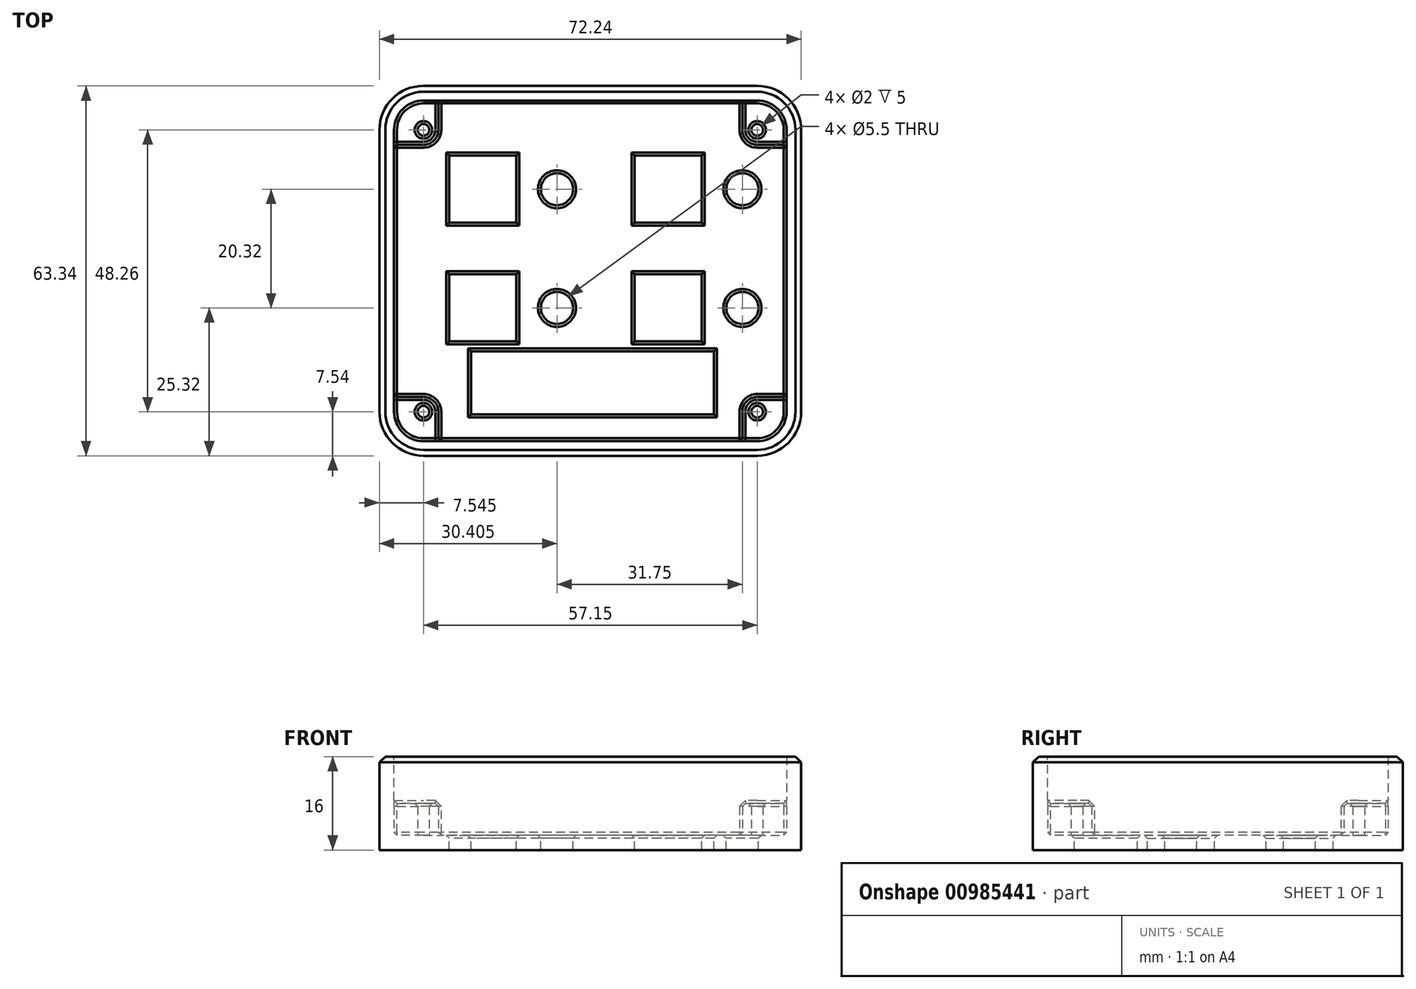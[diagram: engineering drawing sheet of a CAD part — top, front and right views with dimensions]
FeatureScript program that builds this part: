
annotation { "Feature Type Name" : "Feature", "Feature Type Description" : "" }
export const myFeature = defineFeature(function(context is Context, id is Id, definition is map)
    precondition{}
    {
        {
            var Q0;
            Q0=qCreatedBy(makeId("Top.planeOp"),FACE);
            var sketch = newSketch(context, id + "F0", { "sketchPlane" : qUnion([Q0])});
            skLineSegment(sketch, "E0.bottom", {"start": v(-28.57, -31.67) * mm, "end": v(28.58, -31.67) * mm});
            skLineSegment(sketch, "E0.top", {"start": v(-28.57, 31.67) * mm, "end": v(28.58, 31.67) * mm});
            skLineSegment(sketch, "E0.left", {"start": v(-36.11, -24.13) * mm, "end": v(-36.12, 24.13) * mm});
            skLineSegment(sketch, "E0.right", {"start": v(36.12, -24.13) * mm, "end": v(36.11, 24.13) * mm});
            skPoint(sketch, "E0.middle", {"position": v(0, 0) * mm});
            skPoint(sketch, "E1.visualSharp", {"position": v(-36.12, 31.67) * mm});
            skArc(sketch, "E1.filletArc", {"start": v(-28.57, 31.67) * mm, "mid": v(-33.9, 29.46) * mm, "end": v(-36.12, 24.13) * mm});
            skPoint(sketch, "E2.visualSharp", {"position": v(36.11, 31.67) * mm});
            skArc(sketch, "E2.filletArc", {"start": v(36.12, 24.13) * mm, "mid": v(33.9, 29.46) * mm, "end": v(28.58, 31.67) * mm});
            skPoint(sketch, "E3.visualSharp", {"position": v(36.12, -31.67) * mm});
            skArc(sketch, "E3.filletArc", {"start": v(28.58, -31.67) * mm, "mid": v(33.9, -29.46) * mm, "end": v(36.12, -24.13) * mm});
            skPoint(sketch, "E4.visualSharp", {"position": v(-36.11, -31.67) * mm});
            skArc(sketch, "E4.filletArc", {"start": v(-36.11, -24.13) * mm, "mid": v(-33.9, -29.46) * mm, "end": v(-28.57, -31.67) * mm});
            skCircle(sketch, "E5", {"center": v(-28.57, 24.13) * mm, "radius": 1 * mm});
            skCircle(sketch, "E6", {"center": v(28.58, 24.13) * mm, "radius": 1 * mm});
            skCircle(sketch, "E7", {"center": v(28.58, -24.13) * mm, "radius": 1 * mm});
            skCircle(sketch, "E8", {"center": v(-28.57, -24.13) * mm, "radius": 1 * mm});
            skLineSegment(sketch, "E9", {"start": v(-26.04, 31.67) * mm, "end": v(-26.04, 24.13) * mm});
            skLineSegment(sketch, "E10", {"start": v(-28.57, 21.6) * mm, "end": v(-36.11, 21.6) * mm});
            skPoint(sketch, "E11.visualSharp", {"position": v(-26.04, 21.6) * mm});
            skArc(sketch, "E11.filletArc", {"start": v(-28.57, 21.6) * mm, "mid": v(-26.78, 22.33) * mm, "end": v(-26.04, 24.13) * mm});
            skLineSegment(sketch, "E12.MirrorCS", {"start": v(26.04, 31.67) * mm, "end": v(26.04, 24.13) * mm});
            skArc(sketch, "E13.MirrorCS", {"start": v(28.57, 21.6) * mm, "mid": v(26.78, 22.33) * mm, "end": v(26.04, 24.13) * mm});
            skLineSegment(sketch, "E14.MirrorCS", {"start": v(28.57, 21.6) * mm, "end": v(36.11, 21.6) * mm});
            skLineSegment(sketch, "E15.MirrorCS", {"start": v(-28.57, -21.6) * mm, "end": v(-36.11, -21.6) * mm});
            skArc(sketch, "E16.MirrorCS", {"start": v(-28.57, -21.6) * mm, "mid": v(-26.78, -22.33) * mm, "end": v(-26.04, -24.13) * mm});
            skLineSegment(sketch, "E17.MirrorCS", {"start": v(-26.04, -31.67) * mm, "end": v(-26.04, -24.13) * mm});
            skLineSegment(sketch, "E18.MirrorCS", {"start": v(28.57, -21.6) * mm, "end": v(36.11, -21.6) * mm});
            skArc(sketch, "E19.MirrorCS", {"start": v(28.57, -21.6) * mm, "mid": v(26.78, -22.33) * mm, "end": v(26.04, -24.13) * mm});
            skLineSegment(sketch, "E20.MirrorCS", {"start": v(26.04, -31.67) * mm, "end": v(26.04, -24.13) * mm});
            skSolve(sketch);
        }
        {
            var Q0;
            {var subQ0=sQuery(id+"F0.wireOp",EDGE,"E4.filletArc");Q0=makeQuery(id+"F0.imprint","IMPRINT",FACE,{"disambiguationData":[TD([[makeQuery(id+"F0.imprint","IMPRINT",EDGE,{"derivedFrom":subQ0}),1.0]])]});}
            var Q1;
            {var subQ4=sQuery(id+"F0.wireOp",EDGE,"E9");Q1=makeQuery(id+"F0.imprint","IMPRINT",FACE,{"disambiguationData":[TD([[makeQuery(id+"F0.imprint","IMPRINT",EDGE,{"derivedFrom":subQ4}),1.0]])]});}
            var Q2;
            {var subQ0=sQuery(id+"F0.wireOp",EDGE,"E1.filletArc");Q2=makeQuery(id+"F0.imprint","IMPRINT",FACE,{"disambiguationData":[TD([[makeQuery(id+"F0.imprint","IMPRINT",EDGE,{"derivedFrom":subQ0}),1.0]])]});}
            var Q3;
            {var subQ1=sQuery(id+"F0.wireOp",EDGE,"E3.filletArc");Q3=makeQuery(id+"F0.imprint","IMPRINT",FACE,{"disambiguationData":[TD([[makeQuery(id+"F0.imprint","IMPRINT",EDGE,{"derivedFrom":subQ1}),1.0]])]});}
            var Q4;
            {var subQ0=sQuery(id+"F0.wireOp",EDGE,"E2.filletArc");Q4=makeQuery(id+"F0.imprint","IMPRINT",FACE,{"disambiguationData":[TD([[makeQuery(id+"F0.imprint","IMPRINT",EDGE,{"derivedFrom":subQ0}),1.0]])]});}
            var Q5;
            Q5=makeQuery(id+"F0.imprint","IMPRINT",FACE,{"disambiguationData":[TD([[makeQuery(id+"F0.imprint","IMPRINT",EDGE,{"derivedFrom":sQuery(id+"F0.wireOp",EDGE,"E7")}),1.0]])]});
            var Q6;
            Q6=makeQuery(id+"F0.imprint","IMPRINT",FACE,{"disambiguationData":[TD([[makeQuery(id+"F0.imprint","IMPRINT",EDGE,{"derivedFrom":sQuery(id+"F0.wireOp",EDGE,"E6")}),1.0]])]});
            var Q7;
            Q7=makeQuery(id+"F0.imprint","IMPRINT",FACE,{"disambiguationData":[TD([[makeQuery(id+"F0.imprint","IMPRINT",EDGE,{"derivedFrom":sQuery(id+"F0.wireOp",EDGE,"E8")}),1.0]])]});
            var Q8;
            Q8=makeQuery(id+"F0.imprint","IMPRINT",FACE,{"disambiguationData":[TD([[makeQuery(id+"F0.imprint","IMPRINT",EDGE,{"derivedFrom":sQuery(id+"F0.wireOp",EDGE,"E5")}),1.0]])]});
            extrude(context, id + "F1", {"entities" : qUnion([Q0, Q1, Q2, Q3, Q4, Q5, Q6, Q7, Q8]), "depth" : 16 * mm, "offsetDistance" : 25 * mm});
        }
        {
            var Q0;
            Q0=makeQuery(id+"F1.opExtrude","CAP_FACE",FACE,{"disambiguationData":[OSD([sQuery(id+"F0.wireOp",EDGE,"E0.bottom"),sQuery(id+"F0.wireOp",EDGE,"E0.top"),sQuery(id+"F0.wireOp",EDGE,"E0.left"),sQuery(id+"F0.wireOp",EDGE,"E0.right"),sQuery(id+"F0.wireOp",EDGE,"E1.filletArc"),sQuery(id+"F0.wireOp",EDGE,"E2.filletArc"),sQuery(id+"F0.wireOp",EDGE,"E3.filletArc"),sQuery(id+"F0.wireOp",EDGE,"E4.filletArc")])],"isStart":false});
            shell(context, id + "F2", {"entities" : qUnion([Q0]), "thickness" : 2.5 * mm});
        }
        {
            var Q0;
            {var subQ1=sQuery(id+"F0.wireOp",EDGE,"E3.filletArc");Q0=makeQuery(id+"F0.imprint","IMPRINT",FACE,{"disambiguationData":[TD([[makeQuery(id+"F0.imprint","IMPRINT",EDGE,{"derivedFrom":subQ1}),1.0]])]});}
            var Q1;
            {var subQ0=sQuery(id+"F0.wireOp",EDGE,"E2.filletArc");Q1=makeQuery(id+"F0.imprint","IMPRINT",FACE,{"disambiguationData":[TD([[makeQuery(id+"F0.imprint","IMPRINT",EDGE,{"derivedFrom":subQ0}),1.0]])]});}
            var Q2;
            {var subQ0=sQuery(id+"F0.wireOp",EDGE,"E1.filletArc");Q2=makeQuery(id+"F0.imprint","IMPRINT",FACE,{"disambiguationData":[TD([[makeQuery(id+"F0.imprint","IMPRINT",EDGE,{"derivedFrom":subQ0}),1.0]])]});}
            var Q3;
            {var subQ0=sQuery(id+"F0.wireOp",EDGE,"E4.filletArc");Q3=makeQuery(id+"F0.imprint","IMPRINT",FACE,{"disambiguationData":[TD([[makeQuery(id+"F0.imprint","IMPRINT",EDGE,{"derivedFrom":subQ0}),1.0]])]});}
            extrude(context, id + "F3", {"entities" : qUnion([Q0, Q1, Q2, Q3]), "operationType" : NewBodyOperationType.ADD, "depth" : 8 * mm, "offsetDistance" : 25 * mm});
        }
        {
            var Q0;
            {var subQ0=sQuery(id+"F0.wireOp",EDGE,"E0.bottom");var subQ1=sQuery(id+"F0.wireOp",EDGE,"E0.top");var subQ2=sQuery(id+"F0.wireOp",EDGE,"E0.left");var subQ3=sQuery(id+"F0.wireOp",EDGE,"E0.right");Q0=makeQuery(id+"F3.boolean.opBoolean","SPLIT",FACE,{"disambiguationData":[TD([makeQuery(id+"F2.opShell","OFFSET_FACE",FACE,{"disambiguationData":[OSD([subQ0])]})])],"derivedFrom":makeQuery(id+"F2.opShell","OFFSET_FACE",FACE,{"disambiguationData":[OSD([subQ0,subQ1,subQ2,subQ3,sQuery(id+"F0.wireOp",EDGE,"E1.filletArc"),sQuery(id+"F0.wireOp",EDGE,"E2.filletArc"),sQuery(id+"F0.wireOp",EDGE,"E3.filletArc"),sQuery(id+"F0.wireOp",EDGE,"E4.filletArc")])]})});}
            var sketch = newSketch(context, id + "F4", { "sketchPlane" : qUnion([Q0])});
            skLineSegment(sketch, "E21.bottom", {"start": v(-20.45, -13.76) * mm, "end": v(21.19, -13.76) * mm});
            skLineSegment(sketch, "E21.top", {"start": v(-20.45, -24.56) * mm, "end": v(21.19, -24.56) * mm});
            skLineSegment(sketch, "E21.left", {"start": v(-20.45, -13.76) * mm, "end": v(-20.45, -24.56) * mm});
            skLineSegment(sketch, "E21.right", {"start": v(21.19, -13.76) * mm, "end": v(21.19, -24.56) * mm});
            skLineSegment(sketch, "E22.bottom", {"start": v(-12.66, 19.72) * mm, "end": v(-24.17, 19.72) * mm});
            skLineSegment(sketch, "E22.top", {"start": v(-12.67, 8.22) * mm, "end": v(-24.17, 8.22) * mm});
            skLineSegment(sketch, "E22.left", {"start": v(-12.66, 19.72) * mm, "end": v(-12.67, 8.22) * mm});
            skLineSegment(sketch, "E22.right", {"start": v(-24.17, 19.72) * mm, "end": v(-24.17, 8.22) * mm});
            skPoint(sketch, "E22.middle", {"position": v(-18.41, 13.97) * mm});
            skCircle(sketch, "E23", {"center": v(-5.71, 13.97) * mm, "radius": 2.75 * mm});
            skLineSegment(sketch, "E24.0.1.0", {"start": v(-12.66, -0.6) * mm, "end": v(-12.67, -12.1) * mm});
            skLineSegment(sketch, "E24.0.1.1", {"start": v(-24.17, -0.6) * mm, "end": v(-24.17, -12.1) * mm});
            skPoint(sketch, "E24.0.1.2", {"position": v(-18.41, -6.35) * mm});
            skLineSegment(sketch, "E24.0.1.3", {"start": v(-12.66, -0.6) * mm, "end": v(-24.17, -0.6) * mm});
            skLineSegment(sketch, "E24.0.1.4", {"start": v(-12.67, -12.1) * mm, "end": v(-24.17, -12.1) * mm});
            skCircle(sketch, "E24.0.1.5", {"center": v(-5.71, -6.35) * mm, "radius": 2.75 * mm});
            skLineSegment(sketch, "E24.1.0.0", {"start": v(19.09, 19.72) * mm, "end": v(19.09, 8.22) * mm});
            skLineSegment(sketch, "E24.1.0.1", {"start": v(7.58, 19.72) * mm, "end": v(7.58, 8.22) * mm});
            skPoint(sketch, "E24.1.0.2", {"position": v(13.34, 13.97) * mm});
            skLineSegment(sketch, "E24.1.0.3", {"start": v(19.09, 19.72) * mm, "end": v(7.58, 19.72) * mm});
            skLineSegment(sketch, "E24.1.0.4", {"start": v(19.08, 8.22) * mm, "end": v(7.58, 8.22) * mm});
            skCircle(sketch, "E24.1.0.5", {"center": v(26.04, 13.97) * mm, "radius": 2.75 * mm});
            skLineSegment(sketch, "E24.1.1.0", {"start": v(19.09, -0.6) * mm, "end": v(19.09, -12.1) * mm});
            skLineSegment(sketch, "E24.1.1.1", {"start": v(7.58, -0.6) * mm, "end": v(7.58, -12.1) * mm});
            skPoint(sketch, "E24.1.1.2", {"position": v(13.34, -6.35) * mm});
            skLineSegment(sketch, "E24.1.1.3", {"start": v(19.09, -0.6) * mm, "end": v(7.58, -0.6) * mm});
            skLineSegment(sketch, "E24.1.1.4", {"start": v(19.08, -12.1) * mm, "end": v(7.58, -12.1) * mm});
            skCircle(sketch, "E24.1.1.5", {"center": v(26.04, -6.35) * mm, "radius": 2.75 * mm});
            skLineSegment(sketch, "E24.direction1", {"start": v(-24.17, 8.22) * mm, "end": v(7.58, 8.22) * mm, "construction": true});
            skLineSegment(sketch, "E24.direction2", {"start": v(-24.17, 8.22) * mm, "end": v(-24.17, -12.1) * mm, "construction": true});
            skSolve(sketch);
        }
        {
            var Q0;
            Q0 = qSketchRegion(id + "F4", true);
            extrude(context, id + "F5", {"entities" : qUnion([Q0]), "operationType" : NewBodyOperationType.REMOVE, "endBound" : BoundingType.THROUGH_ALL, "oppositeDirection" : true, "depth" : 25 * mm, "offsetDistance" : 25 * mm});
        }
        {
            var Q0;
            Q0=makeQuery(id+"F1.opExtrude","CAP_EDGE",EDGE,{"disambiguationData":[OSD([sQuery(id+"F0.wireOp",EDGE,"E0.left")])],"isStart":false});
            chamfer(context, id + "F6", {"entities" : qUnion([Q0]), "width" : 1 * mm, "tangentPropagation" : true});
        }
        {
            var Q0;
            Q0=makeQuery(id+"F3.opExtrude","CAP_FACE",FACE,{"disambiguationData":[OSD([sQuery(id+"F0.wireOp",EDGE,"E0.top"),sQuery(id+"F0.wireOp",EDGE,"E0.left"),sQuery(id+"F0.wireOp",EDGE,"E1.filletArc"),sQuery(id+"F0.wireOp",EDGE,"E5"),sQuery(id+"F0.wireOp",EDGE,"E9"),sQuery(id+"F0.wireOp",EDGE,"E10"),sQuery(id+"F0.wireOp",EDGE,"E11.filletArc")])],"isStart":false});
            var Q1;
            Q1=makeQuery(id+"F3.opExtrude","CAP_FACE",FACE,{"disambiguationData":[OSD([sQuery(id+"F0.wireOp",EDGE,"E0.top"),sQuery(id+"F0.wireOp",EDGE,"E0.right"),sQuery(id+"F0.wireOp",EDGE,"E2.filletArc"),sQuery(id+"F0.wireOp",EDGE,"E6"),sQuery(id+"F0.wireOp",EDGE,"E12.MirrorCS"),sQuery(id+"F0.wireOp",EDGE,"E13.MirrorCS"),sQuery(id+"F0.wireOp",EDGE,"E14.MirrorCS")])],"isStart":false});
            var Q2;
            Q2=makeQuery(id+"F3.opExtrude","CAP_FACE",FACE,{"disambiguationData":[OSD([sQuery(id+"F0.wireOp",EDGE,"E0.bottom"),sQuery(id+"F0.wireOp",EDGE,"E0.right"),sQuery(id+"F0.wireOp",EDGE,"E3.filletArc"),sQuery(id+"F0.wireOp",EDGE,"E7"),sQuery(id+"F0.wireOp",EDGE,"E18.MirrorCS"),sQuery(id+"F0.wireOp",EDGE,"E19.MirrorCS"),sQuery(id+"F0.wireOp",EDGE,"E20.MirrorCS")])],"isStart":false});
            var Q3;
            Q3=makeQuery(id+"F3.opExtrude","CAP_FACE",FACE,{"disambiguationData":[OSD([sQuery(id+"F0.wireOp",EDGE,"E0.bottom"),sQuery(id+"F0.wireOp",EDGE,"E0.left"),sQuery(id+"F0.wireOp",EDGE,"E4.filletArc"),sQuery(id+"F0.wireOp",EDGE,"E8"),sQuery(id+"F0.wireOp",EDGE,"E15.MirrorCS"),sQuery(id+"F0.wireOp",EDGE,"E16.MirrorCS"),sQuery(id+"F0.wireOp",EDGE,"E17.MirrorCS")])],"isStart":false});
            var Q4;
            {var subQ0=sQuery(id+"F0.wireOp",EDGE,"E0.bottom");var subQ1=sQuery(id+"F0.wireOp",EDGE,"E0.top");var subQ2=sQuery(id+"F0.wireOp",EDGE,"E0.left");var subQ3=sQuery(id+"F0.wireOp",EDGE,"E0.right");Q4=makeQuery(id+"F3.boolean.opBoolean","SPLIT",FACE,{"disambiguationData":[TD([makeQuery(id+"F2.opShell","OFFSET_FACE",FACE,{"disambiguationData":[OSD([subQ0])]})])],"derivedFrom":makeQuery(id+"F2.opShell","OFFSET_FACE",FACE,{"disambiguationData":[OSD([subQ0,subQ1,subQ2,subQ3,sQuery(id+"F0.wireOp",EDGE,"E1.filletArc"),sQuery(id+"F0.wireOp",EDGE,"E2.filletArc"),sQuery(id+"F0.wireOp",EDGE,"E3.filletArc"),sQuery(id+"F0.wireOp",EDGE,"E4.filletArc")])]})});}
            chamfer(context, id + "F7", {"entities" : qUnion([Q0, Q1, Q2, Q3, Q4]), "width" : .5 * mm, "tangentPropagation" : true});
        }
    });
